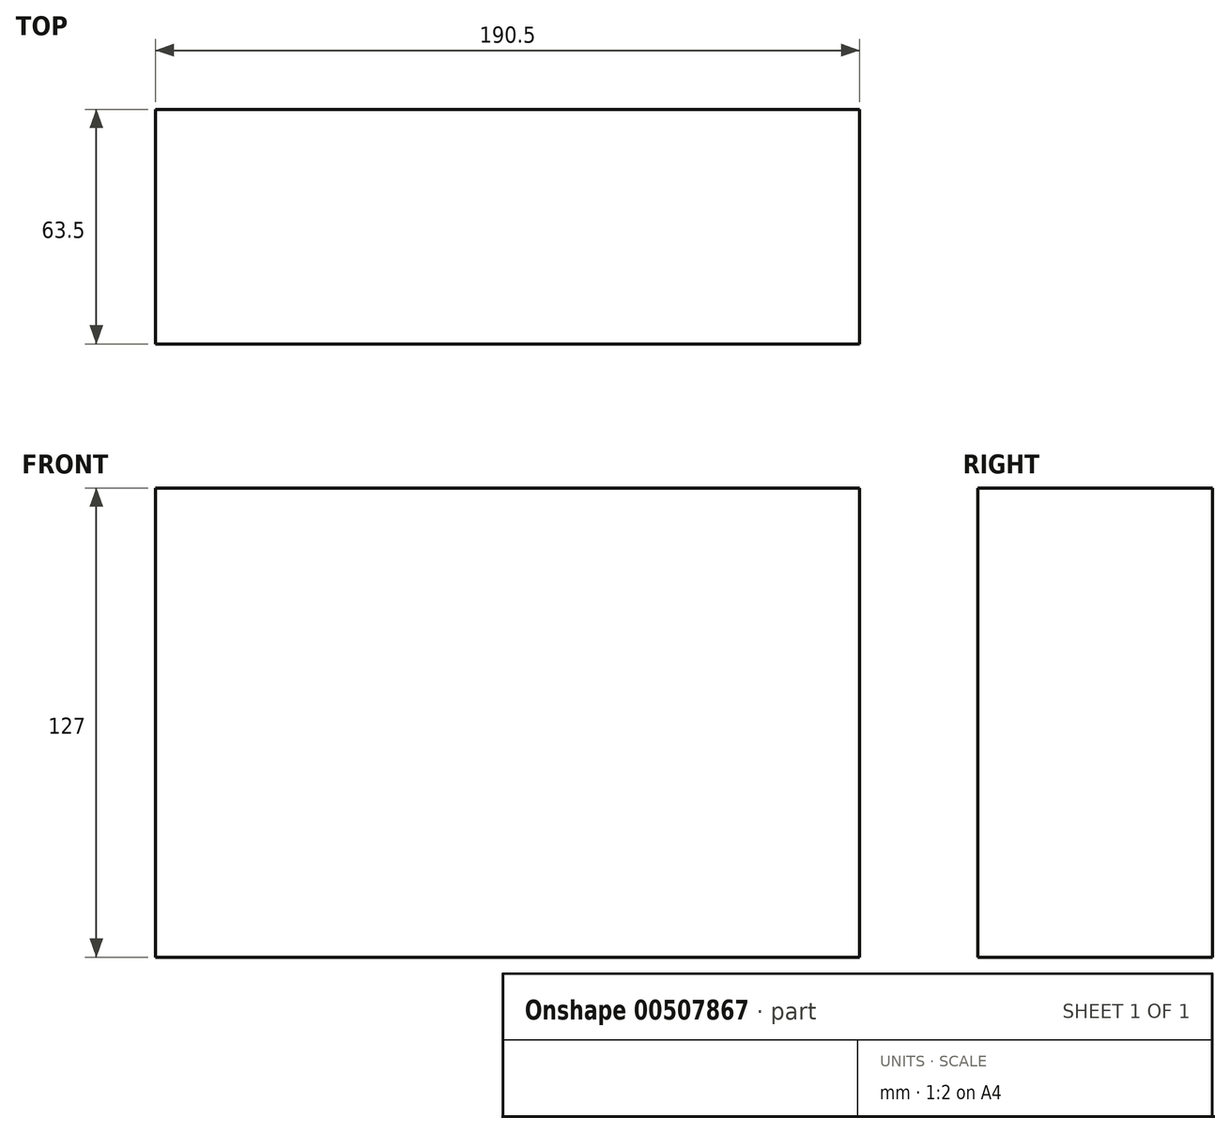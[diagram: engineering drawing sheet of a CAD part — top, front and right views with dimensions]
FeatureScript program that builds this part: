
annotation { "Feature Type Name" : "Feature", "Feature Type Description" : "" }
export const myFeature = defineFeature(function(context is Context, id is Id, definition is map)
    precondition{}
    {
        {
            var Q0;
            Q0=qCreatedBy(makeId("Top.planeOp"),FACE);
            var sketch = newSketch(context, id + "F0", { "sketchPlane" : qUnion([Q0])});
            skLineSegment(sketch, "E0.bottom", {"start": v(-95.25, 31.75) * mm, "end": v(95.25, 31.75) * mm});
            skLineSegment(sketch, "E0.top", {"start": v(-95.25, -31.75) * mm, "end": v(95.25, -31.75) * mm});
            skLineSegment(sketch, "E0.left", {"start": v(-95.25, 31.75) * mm, "end": v(-95.25, -31.75) * mm});
            skLineSegment(sketch, "E0.right", {"start": v(95.25, 31.75) * mm, "end": v(95.25, -31.75) * mm});
            skPoint(sketch, "E0.middle", {"position": v(0, 0) * mm});
            skSolve(sketch);
        }
        {
            var Q0;
            Q0 = qSketchRegion(id + "F0", true);
            extrude(context, id + "F1", {"entities" : qUnion([Q0]), "depth" : 127 * mm});
        }
        {
            var Q0;
            Q0=qCreatedBy(makeId("Top.planeOp"),FACE);
            cPlane(context, id + "F2", {"entities" : qUnion([Q0]), "cplaneType" : CPlaneType.OFFSET, "offset" : 203.2 * mm, "width" : 152.4 * mm, "height" : 152.4 * mm});
        }
    });
